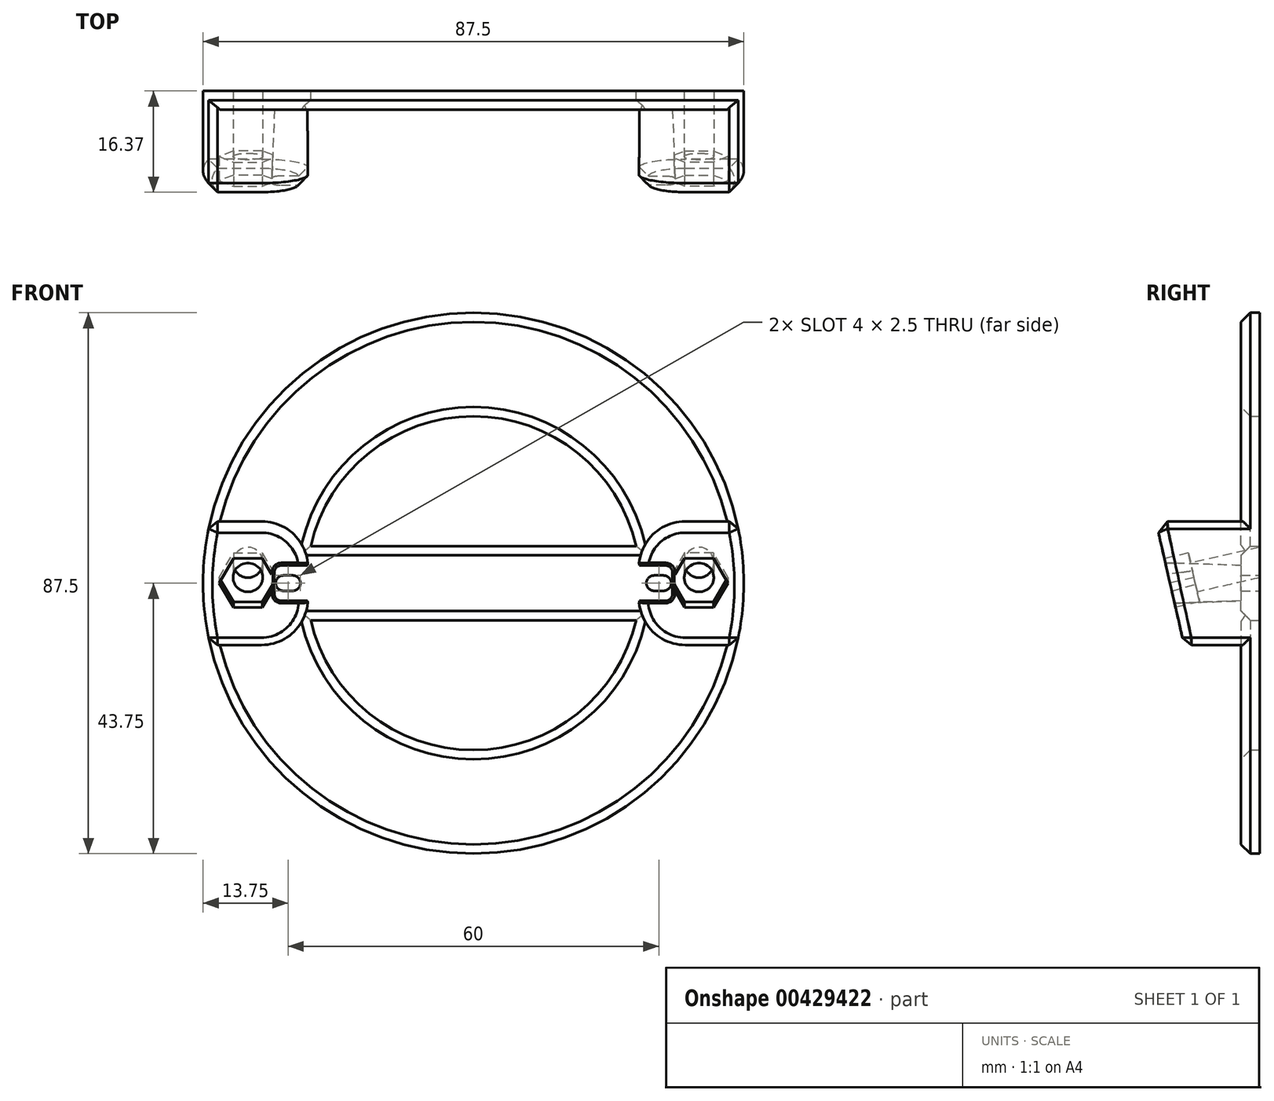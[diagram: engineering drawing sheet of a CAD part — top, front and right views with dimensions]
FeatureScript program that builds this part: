
annotation { "Feature Type Name" : "Feature", "Feature Type Description" : "" }
export const myFeature = defineFeature(function(context is Context, id is Id, definition is map)
    precondition{}
    {
        {
            var Q0;
            Q0=qCreatedBy(makeId("Front.planeOp"),FACE);
            var sketch = newSketch(context, id + "F0", { "sketchPlane" : qUnion([Q0])});
            skCircle(sketch, "E0", {"center": v(0, 0) * mm, "radius": 43.75 * mm});
            skCircle(sketch, "E1", {"center": v(0, 0) * mm, "radius": 24 * mm});
            skSolve(sketch);
        }
        {
            var Q0;
            Q0=makeQuery(id+"F0.imprint","IMPRINT",FACE,{"disambiguationData":[TD([[makeQuery(id+"F0.imprint","IMPRINT",EDGE,{"derivedFrom":sQuery(id+"F0.wireOp",EDGE,"E0")}),1.0]])]});
            extrude(context, id + "F1", {"entities" : qUnion([Q0]), "depth" : 30 * mm});
        }
        {
            var Q0;
            Q0=qCreatedBy(makeId("Right.planeOp"),FACE);
            var sketch = newSketch(context, id + "F2", { "sketchPlane" : qUnion([Q0])});
            skLineSegment(sketch, "E2", {"start": v(0, 43.75) * mm, "end": v(-24.5, 43.75) * mm});
            skLineSegment(sketch, "E3", {"start": v(-24.5, 43.75) * mm, "end": v(-4.5, -43.75) * mm});
            skLineSegment(sketch, "E4", {"start": v(-4.5, -43.75) * mm, "end": v(0, -43.75) * mm});
            skLineSegment(sketch, "E5", {"start": v(0, -43.75) * mm, "end": v(0, 43.75) * mm});
            skSolve(sketch);
        }
        {
            var Q0;
            Q0 = qSketchRegion(id + "F2", true);
            extrude(context, id + "F3", {"entities" : qUnion([Q0]), "endBound" : BoundingType.SYMMETRIC, "depth" : 90 * mm});
        }
        {
            var Q0;
            Q0=makeQuery(id+"F3.opExtrude","SWEPT_BODY",BODY,{"disambiguationData":[OSD([sQuery(id+"F2.wireOp",EDGE,"E2"),sQuery(id+"F2.wireOp",EDGE,"E3"),sQuery(id+"F2.wireOp",EDGE,"E4"),sQuery(id+"F2.wireOp",EDGE,"E5")])]});
            var Q1;
            Q1=makeQuery(id+"F1.opExtrude","SWEPT_BODY",BODY,{"disambiguationData":[OSD([sQuery(id+"F0.wireOp",EDGE,"E0"),sQuery(id+"F0.wireOp",EDGE,"E1")])]});
            booleanBodies(context, id + "F4", {"operationType" : BooleanOperationType.INTERSECTION, "tools" : qUnion([Q0, Q1])});
        }
        {
            var Q0;
            Q0=qCreatedBy(makeId("Front.planeOp"),FACE);
            var sketch = newSketch(context, id + "F5", { "sketchPlane" : qUnion([Q0])});
            skLineSegment(sketch, "E6.bottom", {"start": v(-50, 10) * mm, "end": v(50, 10) * mm});
            skLineSegment(sketch, "E6.top", {"start": v(-50, -10) * mm, "end": v(50, -10) * mm});
            skLineSegment(sketch, "E6.left", {"start": v(-50, 10) * mm, "end": v(-50, -10) * mm});
            skLineSegment(sketch, "E6.right", {"start": v(50, 10) * mm, "end": v(50, -10) * mm});
            skCircle(sketch, "E7", {"center": v(0, 0) * mm, "radius": 27 * mm});
            skSolve(sketch);
        }
        {
            var Q0;
            {var subQ0=sQuery(id+"F5.wireOp",EDGE,"E6.left");Q0=makeQuery(id+"F5.imprint","IMPRINT",FACE,{"disambiguationData":[TD([[makeQuery(id+"F5.imprint","IMPRINT",EDGE,{"derivedFrom":subQ0}),1.0]])]});}
            var Q1;
            {var subQ0=sQuery(id+"F5.wireOp",EDGE,"E6.right");Q1=makeQuery(id+"F5.imprint","IMPRINT",FACE,{"disambiguationData":[TD([[makeQuery(id+"F5.imprint","IMPRINT",EDGE,{"derivedFrom":subQ0}),-1.0]])]});}
            extrude(context, id + "F6", {"entities" : qUnion([Q0, Q1]), "depth" : 30 * mm});
        }
        {
            var Q0;
            Q0=makeQuery(id+"F6.opExtrude","SWEPT_BODY",BODY,{"disambiguationData":[OSD([sQuery(id+"F5.wireOp",EDGE,"E6.bottom"),sQuery(id+"F5.wireOp",EDGE,"E6.top"),sQuery(id+"F5.wireOp",EDGE,"E6.left"),sQuery(id+"F5.wireOp",EDGE,"E7")])]});
            var Q1;
            Q1=makeQuery(id+"F4.opBoolean","INTERSECT",BODY,{"derivedFrom":[makeQuery(id+"F1.opExtrude","SWEPT_BODY",BODY,{"disambiguationData":[OSD([sQuery(id+"F0.wireOp",EDGE,"E0"),sQuery(id+"F0.wireOp",EDGE,"E1")])]}),makeQuery(id+"F3.opExtrude","SWEPT_BODY",BODY,{"disambiguationData":[OSD([sQuery(id+"F2.wireOp",EDGE,"E2"),sQuery(id+"F2.wireOp",EDGE,"E3"),sQuery(id+"F2.wireOp",EDGE,"E4"),sQuery(id+"F2.wireOp",EDGE,"E5")])]})]});
            booleanBodies(context, id + "F7", {"operationType" : BooleanOperationType.INTERSECTION, "tools" : qUnion([Q0, Q1]), "keepTools" : true});
        }
        {
            var Q0;
            Q0=makeQuery(id+"F4.opBoolean","INTERSECT",BODY,{"derivedFrom":[makeQuery(id+"F1.opExtrude","SWEPT_BODY",BODY,{"disambiguationData":[OSD([sQuery(id+"F0.wireOp",EDGE,"E0"),sQuery(id+"F0.wireOp",EDGE,"E1")])]}),makeQuery(id+"F3.opExtrude","SWEPT_BODY",BODY,{"disambiguationData":[OSD([sQuery(id+"F2.wireOp",EDGE,"E2"),sQuery(id+"F2.wireOp",EDGE,"E3"),sQuery(id+"F2.wireOp",EDGE,"E4"),sQuery(id+"F2.wireOp",EDGE,"E5")])]})]});
            var Q1;
            Q1=makeQuery(id+"F6.opExtrude","SWEPT_BODY",BODY,{"disambiguationData":[OSD([sQuery(id+"F5.wireOp",EDGE,"E6.bottom"),sQuery(id+"F5.wireOp",EDGE,"E6.top"),sQuery(id+"F5.wireOp",EDGE,"E6.right"),sQuery(id+"F5.wireOp",EDGE,"E7")])]});
            booleanBodies(context, id + "F8", {"operationType" : BooleanOperationType.INTERSECTION, "tools" : qUnion([Q0, Q1])});
        }
        {
            var Q0;
            Q0=qCreatedBy(makeId("Front.planeOp"),FACE);
            var sketch = newSketch(context, id + "F9", { "sketchPlane" : qUnion([Q0])});
            skCircle(sketch, "E8", {"center": v(0, 0) * mm, "radius": 43.75 * mm});
            skCircle(sketch, "E9", {"center": v(0, 0) * mm, "radius": 27 * mm});
            skLineSegment(sketch, "E10.bottom", {"start": v(-26.32, 6) * mm, "end": v(26.32, 6) * mm});
            skLineSegment(sketch, "E10.top", {"start": v(-26.32, -6) * mm, "end": v(26.32, -6) * mm});
            skPoint(sketch, "E11", {"position": v(-26.32, 6) * mm});
            skPoint(sketch, "E12", {"position": v(-26.32, -6) * mm});
            skPoint(sketch, "E13", {"position": v(26.32, 6) * mm});
            skPoint(sketch, "E14", {"position": v(26.32, -6) * mm});
            skSolve(sketch);
        }
        {
            var Q0;
            Q0=makeQuery(id+"F9.imprint","IMPRINT",FACE,{"disambiguationData":[TD([[makeQuery(id+"F9.imprint","IMPRINT",EDGE,{"derivedFrom":sQuery(id+"F9.wireOp",EDGE,"E8")}),1.0]])]});
            var Q1;
            {var subQ0=sQuery(id+"F9.wireOp",EDGE,"E10.bottom");Q1=makeQuery(id+"F9.imprint","IMPRINT",FACE,{"disambiguationData":[TD([[makeQuery(id+"F9.imprint","IMPRINT",EDGE,{"derivedFrom":subQ0}),-1.0]])]});}
            extrude(context, id + "F10", {"entities" : qUnion([Q0, Q1]), "depth" : 3 * mm});
        }
        {
            var Q0;
            Q0=qCreatedBy(makeId("Front.planeOp"),FACE);
            var sketch = newSketch(context, id + "F11", { "sketchPlane" : qUnion([Q0])});
            skLineSegment(sketch, "E15.bottom", {"start": v(-29.25, 1.25) * mm, "end": v(-30.75, 1.25) * mm});
            skLineSegment(sketch, "E15.top", {"start": v(-29.25, -1.25) * mm, "end": v(-30.75, -1.25) * mm});
            skLineSegment(sketch, "E15.left", {"start": v(-28, 0) * mm, "end": v(-28, 0) * mm});
            skLineSegment(sketch, "E15.right", {"start": v(-32, 0) * mm, "end": v(-32, 0) * mm});
            skPoint(sketch, "E15.middle", {"position": v(-30, 0) * mm});
            skPoint(sketch, "E16.visualSharp", {"position": v(-28, 1.25) * mm});
            skArc(sketch, "E16.filletArc", {"start": v(-28, 0) * mm, "mid": v(-28.37, 0.88) * mm, "end": v(-29.25, 1.25) * mm});
            skPoint(sketch, "E17.visualSharp", {"position": v(-32, 1.25) * mm});
            skArc(sketch, "E17.filletArc", {"start": v(-30.75, 1.25) * mm, "mid": v(-31.63, 0.88) * mm, "end": v(-32, 0) * mm});
            skPoint(sketch, "E18.visualSharp", {"position": v(-32, -1.25) * mm});
            skArc(sketch, "E18.filletArc", {"start": v(-32, 0) * mm, "mid": v(-31.63, -0.88) * mm, "end": v(-30.75, -1.25) * mm});
            skPoint(sketch, "E19.visualSharp", {"position": v(-28, -1.25) * mm});
            skArc(sketch, "E19.filletArc", {"start": v(-29.25, -1.25) * mm, "mid": v(-28.37, -0.88) * mm, "end": v(-28, 0) * mm});
            skArc(sketch, "E20.MirrorCS", {"start": v(28, 0) * mm, "mid": v(28.37, 0.88) * mm, "end": v(29.25, 1.25) * mm});
            skArc(sketch, "E21.MirrorCS", {"start": v(29.25, -1.25) * mm, "mid": v(28.37, -0.88) * mm, "end": v(28, 0) * mm});
            skLineSegment(sketch, "E22.MirrorCS", {"start": v(29.25, -1.25) * mm, "end": v(30.75, -1.25) * mm});
            skLineSegment(sketch, "E23.MirrorCS", {"start": v(29.25, 1.25) * mm, "end": v(30.75, 1.25) * mm});
            skPoint(sketch, "E24.MirrorP", {"position": v(32, 1.25) * mm});
            skArc(sketch, "E25.MirrorCS", {"start": v(30.75, 1.25) * mm, "mid": v(31.63, 0.88) * mm, "end": v(32, 0) * mm});
            skArc(sketch, "E26.MirrorCS", {"start": v(32, 0) * mm, "mid": v(31.63, -0.88) * mm, "end": v(30.75, -1.25) * mm});
            skPoint(sketch, "E27.MirrorP", {"position": v(32, -1.25) * mm});
            skPoint(sketch, "E28.MirrorP", {"position": v(28, -1.25) * mm});
            skPoint(sketch, "E29.MirrorP", {"position": v(28, 1.25) * mm});
            skSolve(sketch);
        }
        {
            var Q0;
            Q0 = qSketchRegion(id + "F11", true);
            extrude(context, id + "F12", {"entities" : qUnion([Q0]), "depth" : 25 * mm});
        }
        {
            var Q0;
            Q0=makeQuery(id+"F6.opExtrude","SWEPT_BODY",BODY,{"disambiguationData":[OSD([sQuery(id+"F5.wireOp",EDGE,"E6.bottom"),sQuery(id+"F5.wireOp",EDGE,"E6.top"),sQuery(id+"F5.wireOp",EDGE,"E6.left"),sQuery(id+"F5.wireOp",EDGE,"E7")])]});
            deleteBodies(context, id + "F13", {"entities" : qUnion([Q0])});
        }
        {
            var Q0;
            Q0=qCreatedBy(makeId("Front.planeOp"),FACE);
            var sketch = newSketch(context, id + "F14", { "sketchPlane" : qUnion([Q0])});
            skLineSegment(sketch, "E30.bottom", {"start": v(-26.55, 2.75) * mm, "end": v(-31.11, 2.75) * mm});
            skLineSegment(sketch, "E30.top", {"start": v(-26.55, -2.75) * mm, "end": v(-31.11, -2.75) * mm});
            skLineSegment(sketch, "E30.left", {"start": v(-24.55, 0.75) * mm, "end": v(-24.55, -0.75) * mm});
            skLineSegment(sketch, "E30.right", {"start": v(-32.11, 1.75) * mm, "end": v(-32.11, -1.75) * mm});
            skPoint(sketch, "E30.middle", {"position": v(-28.33, 0) * mm});
            skPoint(sketch, "E31.visualSharp", {"position": v(-24.55, 2.75) * mm});
            skArc(sketch, "E31.filletArc", {"start": v(-24.55, 0.75) * mm, "mid": v(-25.13, 2.16) * mm, "end": v(-26.55, 2.75) * mm});
            skPoint(sketch, "E32.visualSharp", {"position": v(-24.55, -2.75) * mm});
            skArc(sketch, "E32.filletArc", {"start": v(-26.55, -2.75) * mm, "mid": v(-25.13, -2.16) * mm, "end": v(-24.55, -0.75) * mm});
            skPoint(sketch, "E33.visualSharp", {"position": v(-32.11, -2.75) * mm});
            skArc(sketch, "E33.filletArc", {"start": v(-32.11, -1.75) * mm, "mid": v(-31.82, -2.46) * mm, "end": v(-31.11, -2.75) * mm});
            skPoint(sketch, "E34.visualSharp", {"position": v(-32.11, 2.75) * mm});
            skArc(sketch, "E34.filletArc", {"start": v(-31.11, 2.75) * mm, "mid": v(-31.82, 2.46) * mm, "end": v(-32.11, 1.75) * mm});
            skArc(sketch, "E35.MirrorCS", {"start": v(31.11, 2.75) * mm, "mid": v(31.82, 2.46) * mm, "end": v(32.11, 1.75) * mm});
            skLineSegment(sketch, "E36.MirrorCS", {"start": v(32.11, 1.75) * mm, "end": v(32.11, -1.75) * mm});
            skArc(sketch, "E37.MirrorCS", {"start": v(32.11, -1.75) * mm, "mid": v(31.82, -2.46) * mm, "end": v(31.11, -2.75) * mm});
            skLineSegment(sketch, "E38.MirrorCS", {"start": v(26.55, 2.75) * mm, "end": v(31.11, 2.75) * mm});
            skLineSegment(sketch, "E39.MirrorCS", {"start": v(26.55, -2.75) * mm, "end": v(31.11, -2.75) * mm});
            skArc(sketch, "E40.MirrorCS", {"start": v(26.55, -2.75) * mm, "mid": v(25.13, -2.16) * mm, "end": v(24.55, -0.75) * mm});
            skArc(sketch, "E41.MirrorCS", {"start": v(24.55, 0.75) * mm, "mid": v(25.13, 2.16) * mm, "end": v(26.55, 2.75) * mm});
            skSolve(sketch);
        }
        {
            var Q0;
            Q0 = qSketchRegion(id + "F14", true);
            extrude(context, id + "F15", {"entities" : qUnion([Q0]), "depth" : 25 * mm, "hasDraft" : true, "draftAngle" : 2 * degree});
        }
        {
            var Q0;
            Q0=makeQuery(id+"F15.opExtrude","SWEPT_BODY",BODY,{"disambiguationData":[OSD([sQuery(id+"F14.wireOp",EDGE,"E30.bottom"),sQuery(id+"F14.wireOp",EDGE,"E30.top"),sQuery(id+"F14.wireOp",EDGE,"E30.left"),sQuery(id+"F14.wireOp",EDGE,"E30.right"),sQuery(id+"F14.wireOp",EDGE,"E31.filletArc"),sQuery(id+"F14.wireOp",EDGE,"E32.filletArc"),sQuery(id+"F14.wireOp",EDGE,"E33.filletArc"),sQuery(id+"F14.wireOp",EDGE,"E34.filletArc")])]});
            var Q1;
            Q1=qCreatedBy(makeId("Right.planeOp"),FACE);
            mirror(context, id + "F16", {"entities" : qUnion([Q0]), "mirrorPlane" : qUnion([Q1])});
        }
        {
            var Q0;
            Q0=makeQuery(id+"F15.opExtrude","SWEPT_BODY",BODY,{"disambiguationData":[OSD([sQuery(id+"F14.wireOp",EDGE,"E30.bottom"),sQuery(id+"F14.wireOp",EDGE,"E30.top"),sQuery(id+"F14.wireOp",EDGE,"E30.left"),sQuery(id+"F14.wireOp",EDGE,"E30.right"),sQuery(id+"F14.wireOp",EDGE,"E31.filletArc"),sQuery(id+"F14.wireOp",EDGE,"E32.filletArc"),sQuery(id+"F14.wireOp",EDGE,"E33.filletArc"),sQuery(id+"F14.wireOp",EDGE,"E34.filletArc")])]});
            var Q1;
            Q1=makeQuery(id+"F7.opBoolean","INTERSECT",BODY,{"derivedFrom":[makeQuery(id+"F4.opBoolean","INTERSECT",BODY,{"derivedFrom":[makeQuery(id+"F1.opExtrude","SWEPT_BODY",BODY,{"disambiguationData":[OSD([sQuery(id+"F0.wireOp",EDGE,"E0"),sQuery(id+"F0.wireOp",EDGE,"E1")])]}),makeQuery(id+"F3.opExtrude","SWEPT_BODY",BODY,{"disambiguationData":[OSD([sQuery(id+"F2.wireOp",EDGE,"E2"),sQuery(id+"F2.wireOp",EDGE,"E3"),sQuery(id+"F2.wireOp",EDGE,"E4"),sQuery(id+"F2.wireOp",EDGE,"E5")])]})]}),makeQuery(id+"F6.opExtrude","SWEPT_BODY",BODY,{"disambiguationData":[OSD([sQuery(id+"F5.wireOp",EDGE,"E6.bottom"),sQuery(id+"F5.wireOp",EDGE,"E6.top"),sQuery(id+"F5.wireOp",EDGE,"E6.left"),sQuery(id+"F5.wireOp",EDGE,"E7")])]})]});
            booleanBodies(context, id + "F17", {"operationType" : BooleanOperationType.SUBTRACTION, "tools" : qUnion([Q0]), "targets" : qUnion([Q1])});
        }
        {
            var Q0;
            Q0=makeQuery(id+"F16.opPattern","COPY",BODY,{"derivedFrom":makeQuery(id+"F15.opExtrude","SWEPT_BODY",BODY,{"disambiguationData":[OSD([sQuery(id+"F14.wireOp",EDGE,"E30.bottom"),sQuery(id+"F14.wireOp",EDGE,"E30.top"),sQuery(id+"F14.wireOp",EDGE,"E30.left"),sQuery(id+"F14.wireOp",EDGE,"E30.right"),sQuery(id+"F14.wireOp",EDGE,"E31.filletArc"),sQuery(id+"F14.wireOp",EDGE,"E32.filletArc"),sQuery(id+"F14.wireOp",EDGE,"E33.filletArc"),sQuery(id+"F14.wireOp",EDGE,"E34.filletArc")])]}),"instanceName":"1"});
            var Q1;
            Q1=makeQuery(id+"F8.opBoolean","INTERSECT",BODY,{"derivedFrom":[makeQuery(id+"F4.opBoolean","INTERSECT",BODY,{"derivedFrom":[makeQuery(id+"F1.opExtrude","SWEPT_BODY",BODY,{"disambiguationData":[OSD([sQuery(id+"F0.wireOp",EDGE,"E0"),sQuery(id+"F0.wireOp",EDGE,"E1")])]}),makeQuery(id+"F3.opExtrude","SWEPT_BODY",BODY,{"disambiguationData":[OSD([sQuery(id+"F2.wireOp",EDGE,"E2"),sQuery(id+"F2.wireOp",EDGE,"E3"),sQuery(id+"F2.wireOp",EDGE,"E4"),sQuery(id+"F2.wireOp",EDGE,"E5")])]})]}),makeQuery(id+"F6.opExtrude","SWEPT_BODY",BODY,{"disambiguationData":[OSD([sQuery(id+"F5.wireOp",EDGE,"E6.bottom"),sQuery(id+"F5.wireOp",EDGE,"E6.top"),sQuery(id+"F5.wireOp",EDGE,"E6.right"),sQuery(id+"F5.wireOp",EDGE,"E7")])]})]});
            booleanBodies(context, id + "F18", {"operationType" : BooleanOperationType.SUBTRACTION, "tools" : qUnion([Q0]), "targets" : qUnion([Q1])});
        }
        {
            var Q0;
            Q0=makeQuery(id+"F12.opExtrude","SWEPT_BODY",BODY,{"disambiguationData":[OSD([sQuery(id+"F11.wireOp",EDGE,"E15.bottom"),sQuery(id+"F11.wireOp",EDGE,"E15.top"),sQuery(id+"F11.wireOp",EDGE,"E16.filletArc"),sQuery(id+"F11.wireOp",EDGE,"E17.filletArc"),sQuery(id+"F11.wireOp",EDGE,"E18.filletArc"),sQuery(id+"F11.wireOp",EDGE,"E19.filletArc")])]});
            var Q1;
            Q1=makeQuery(id+"F12.opExtrude","SWEPT_BODY",BODY,{"disambiguationData":[OSD([sQuery(id+"F11.wireOp",EDGE,"E20.MirrorCS"),sQuery(id+"F11.wireOp",EDGE,"E21.MirrorCS"),sQuery(id+"F11.wireOp",EDGE,"E22.MirrorCS"),sQuery(id+"F11.wireOp",EDGE,"E23.MirrorCS"),sQuery(id+"F11.wireOp",EDGE,"E25.MirrorCS"),sQuery(id+"F11.wireOp",EDGE,"E26.MirrorCS")])]});
            var Q2;
            Q2=makeQuery(id+"F10.opExtrude","SWEPT_BODY",BODY,{"disambiguationData":[OSD([sQuery(id+"F9.wireOp",EDGE,"E8"),sQuery(id+"F9.wireOp",EDGE,"E9"),sQuery(id+"F9.wireOp",EDGE,"E10.bottom"),sQuery(id+"F9.wireOp",EDGE,"E10.top")])]});
            booleanBodies(context, id + "F19", {"operationType" : BooleanOperationType.SUBTRACTION, "tools" : qUnion([Q0, Q1]), "targets" : qUnion([Q2])});
        }
        {
            var Q0;
            Q0=makeQuery(id+"F7.opBoolean","COPY",FACE,{"derivedFrom":makeQuery(id+"F3.opExtrude","SWEPT_FACE",FACE,{"disambiguationData":[OSD([sQuery(id+"F2.wireOp",EDGE,"E3")])]})});
            var sketch = newSketch(context, id + "F20", { "sketchPlane" : qUnion([Q0])});
            skCircle(sketch, "E42.cCircle", {"center": v(-36.5, 3.27) * mm, "radius": 4.05 * mm, "construction": true});
            skLineSegment(sketch, "E42.0", {"start": v(-38.84, 7.32) * mm, "end": v(-34.16, 7.32) * mm});
            skLineSegment(sketch, "E42.1", {"start": v(-34.16, 7.32) * mm, "end": v(-31.82, 3.27) * mm});
            skLineSegment(sketch, "E42.2", {"start": v(-31.82, 3.27) * mm, "end": v(-34.16, -0.78) * mm});
            skLineSegment(sketch, "E42.3", {"start": v(-34.16, -0.78) * mm, "end": v(-38.84, -0.78) * mm});
            skLineSegment(sketch, "E42.4", {"start": v(-38.84, -0.78) * mm, "end": v(-41.18, 3.27) * mm});
            skLineSegment(sketch, "E42.5", {"start": v(-41.18, 3.27) * mm, "end": v(-38.84, 7.32) * mm});
            skPoint(sketch, "E42.0.midPoint", {"position": v(-36.5, 7.32) * mm});
            skSolve(sketch);
        }
        {
            var Q0;
            Q0 = qSketchRegion(id + "F20", true);
            extrude(context, id + "F21", {"entities" : qUnion([Q0]), "operationType" : NewBodyOperationType.REMOVE, "oppositeDirection" : true, "depth" : 4 * mm});
        }
        {
            var Q0;
            Q0=makeQuery(id+"F7.opBoolean","INTERSECT",BODY,{"derivedFrom":[makeQuery(id+"F4.opBoolean","INTERSECT",BODY,{"derivedFrom":[makeQuery(id+"F1.opExtrude","SWEPT_BODY",BODY,{"disambiguationData":[OSD([sQuery(id+"F0.wireOp",EDGE,"E0"),sQuery(id+"F0.wireOp",EDGE,"E1")])]}),makeQuery(id+"F3.opExtrude","SWEPT_BODY",BODY,{"disambiguationData":[OSD([sQuery(id+"F2.wireOp",EDGE,"E2"),sQuery(id+"F2.wireOp",EDGE,"E3"),sQuery(id+"F2.wireOp",EDGE,"E4"),sQuery(id+"F2.wireOp",EDGE,"E5")])]})]}),makeQuery(id+"F6.opExtrude","SWEPT_BODY",BODY,{"disambiguationData":[OSD([sQuery(id+"F5.wireOp",EDGE,"E6.bottom"),sQuery(id+"F5.wireOp",EDGE,"E6.top"),sQuery(id+"F5.wireOp",EDGE,"E6.left"),sQuery(id+"F5.wireOp",EDGE,"E7")])]})]});
            var Q1;
            Q1=qCreatedBy(makeId("Right.planeOp"),FACE);
            mirror(context, id + "F22", {"entities" : qUnion([Q0]), "mirrorPlane" : qUnion([Q1])});
        }
        {
            var Q0;
            Q0=makeQuery(id+"F8.opBoolean","INTERSECT",BODY,{"derivedFrom":[makeQuery(id+"F4.opBoolean","INTERSECT",BODY,{"derivedFrom":[makeQuery(id+"F1.opExtrude","SWEPT_BODY",BODY,{"disambiguationData":[OSD([sQuery(id+"F0.wireOp",EDGE,"E0"),sQuery(id+"F0.wireOp",EDGE,"E1")])]}),makeQuery(id+"F3.opExtrude","SWEPT_BODY",BODY,{"disambiguationData":[OSD([sQuery(id+"F2.wireOp",EDGE,"E2"),sQuery(id+"F2.wireOp",EDGE,"E3"),sQuery(id+"F2.wireOp",EDGE,"E4"),sQuery(id+"F2.wireOp",EDGE,"E5")])]})]}),makeQuery(id+"F6.opExtrude","SWEPT_BODY",BODY,{"disambiguationData":[OSD([sQuery(id+"F5.wireOp",EDGE,"E6.bottom"),sQuery(id+"F5.wireOp",EDGE,"E6.top"),sQuery(id+"F5.wireOp",EDGE,"E6.right"),sQuery(id+"F5.wireOp",EDGE,"E7")])]})]});
            deleteBodies(context, id + "F23", {"entities" : qUnion([Q0])});
        }
        {
            var Q0;
            Q0=makeQuery(id+"F7.opBoolean","COPY",FACE,{"derivedFrom":makeQuery(id+"F3.opExtrude","SWEPT_FACE",FACE,{"disambiguationData":[OSD([sQuery(id+"F2.wireOp",EDGE,"E3")])]})});
            var sketch = newSketch(context, id + "F24", { "sketchPlane" : qUnion([Q0])});
            skCircle(sketch, "E43", {"center": v(-36.5, 3.27) * mm, "radius": 2.4 * mm});
            skCircle(sketch, "E44.MirrorC", {"center": v(36.5, 3.27) * mm, "radius": 2.4 * mm});
            skSolve(sketch);
        }
        {
            var Q0;
            Q0 = qSketchRegion(id + "F24", true);
            extrude(context, id + "F25", {"entities" : qUnion([Q0]), "oppositeDirection" : true, "depth" : 17 * mm});
        }
        {
            var Q0;
            {var subQ0=sQuery(id+"F5.wireOp",EDGE,"E7");var subQ1=sQuery(id+"F5.wireOp",EDGE,"E6.bottom");Q0=makeQuery(id+"F22.opPattern","COPY",EDGE,{"derivedFrom":makeQuery(id+"F7.opBoolean","COPY",EDGE,{"derivedFrom":makeQuery(id+"F6.opExtrude","SWEPT_EDGE",EDGE,{"disambiguationData":[OSD([subQ1,subQ0]),TDD([makeQuery(id+"F5.imprint","INTERSECT",VERTEX,{"disambiguationData":[OD(0.0)],"derivedFrom":[subQ1,subQ0]})])]})}),"instanceName":"1"});}
            var Q1;
            {var subQ0=sQuery(id+"F5.wireOp",EDGE,"E7");var subQ1=sQuery(id+"F5.wireOp",EDGE,"E6.top");Q1=makeQuery(id+"F22.opPattern","COPY",EDGE,{"derivedFrom":makeQuery(id+"F7.opBoolean","COPY",EDGE,{"derivedFrom":makeQuery(id+"F6.opExtrude","SWEPT_EDGE",EDGE,{"disambiguationData":[OSD([subQ1,subQ0]),TDD([makeQuery(id+"F5.imprint","INTERSECT",VERTEX,{"disambiguationData":[OD(0.0)],"derivedFrom":[subQ1,subQ0]})])]})}),"instanceName":"1"});}
            var Q2;
            {var subQ0=sQuery(id+"F5.wireOp",EDGE,"E7");var subQ1=sQuery(id+"F5.wireOp",EDGE,"E6.bottom");Q2=makeQuery(id+"F7.opBoolean","COPY",EDGE,{"derivedFrom":makeQuery(id+"F6.opExtrude","SWEPT_EDGE",EDGE,{"disambiguationData":[OSD([subQ1,subQ0]),TDD([makeQuery(id+"F5.imprint","INTERSECT",VERTEX,{"disambiguationData":[OD(0.0)],"derivedFrom":[subQ1,subQ0]})])]})});}
            var Q3;
            {var subQ0=sQuery(id+"F5.wireOp",EDGE,"E7");var subQ1=sQuery(id+"F5.wireOp",EDGE,"E6.top");Q3=makeQuery(id+"F7.opBoolean","COPY",EDGE,{"derivedFrom":makeQuery(id+"F6.opExtrude","SWEPT_EDGE",EDGE,{"disambiguationData":[OSD([subQ1,subQ0]),TDD([makeQuery(id+"F5.imprint","INTERSECT",VERTEX,{"disambiguationData":[OD(0.0)],"derivedFrom":[subQ1,subQ0]})])]})});}
            fillet(context, id + "F26", {"entities" : qUnion([Q0, Q1, Q2, Q3]), "radius" : 7.5 * mm, "tangentPropagation" : true, "allowEdgeOverflow" : false});
        }
        {
            var Q0;
            Q0=makeQuery(id+"F10.opExtrude","SWEPT_BODY",BODY,{"disambiguationData":[OSD([sQuery(id+"F9.wireOp",EDGE,"E8"),sQuery(id+"F9.wireOp",EDGE,"E9"),sQuery(id+"F9.wireOp",EDGE,"E10.bottom"),sQuery(id+"F9.wireOp",EDGE,"E10.top")])]});
            var Q1;
            Q1=makeQuery(id+"F7.opBoolean","INTERSECT",BODY,{"derivedFrom":[makeQuery(id+"F4.opBoolean","INTERSECT",BODY,{"derivedFrom":[makeQuery(id+"F1.opExtrude","SWEPT_BODY",BODY,{"disambiguationData":[OSD([sQuery(id+"F0.wireOp",EDGE,"E0"),sQuery(id+"F0.wireOp",EDGE,"E1")])]}),makeQuery(id+"F3.opExtrude","SWEPT_BODY",BODY,{"disambiguationData":[OSD([sQuery(id+"F2.wireOp",EDGE,"E2"),sQuery(id+"F2.wireOp",EDGE,"E3"),sQuery(id+"F2.wireOp",EDGE,"E4"),sQuery(id+"F2.wireOp",EDGE,"E5")])]})]}),makeQuery(id+"F6.opExtrude","SWEPT_BODY",BODY,{"disambiguationData":[OSD([sQuery(id+"F5.wireOp",EDGE,"E6.bottom"),sQuery(id+"F5.wireOp",EDGE,"E6.top"),sQuery(id+"F5.wireOp",EDGE,"E6.left"),sQuery(id+"F5.wireOp",EDGE,"E7")])]})]});
            var Q2;
            Q2=makeQuery(id+"F22.opPattern","COPY",BODY,{"derivedFrom":makeQuery(id+"F7.opBoolean","INTERSECT",BODY,{"derivedFrom":[makeQuery(id+"F4.opBoolean","INTERSECT",BODY,{"derivedFrom":[makeQuery(id+"F1.opExtrude","SWEPT_BODY",BODY,{"disambiguationData":[OSD([sQuery(id+"F0.wireOp",EDGE,"E0"),sQuery(id+"F0.wireOp",EDGE,"E1")])]}),makeQuery(id+"F3.opExtrude","SWEPT_BODY",BODY,{"disambiguationData":[OSD([sQuery(id+"F2.wireOp",EDGE,"E2"),sQuery(id+"F2.wireOp",EDGE,"E3"),sQuery(id+"F2.wireOp",EDGE,"E4"),sQuery(id+"F2.wireOp",EDGE,"E5")])]})]}),makeQuery(id+"F6.opExtrude","SWEPT_BODY",BODY,{"disambiguationData":[OSD([sQuery(id+"F5.wireOp",EDGE,"E6.bottom"),sQuery(id+"F5.wireOp",EDGE,"E6.top"),sQuery(id+"F5.wireOp",EDGE,"E6.left"),sQuery(id+"F5.wireOp",EDGE,"E7")])]})]}),"instanceName":"1"});
            booleanBodies(context, id + "F27", {"operationType" : BooleanOperationType.UNION, "tools" : qUnion([Q0, Q1, Q2])});
        }
        {
            var Q0;
            Q0=makeQuery(id+"F25.opExtrude","SWEPT_BODY",BODY,{"disambiguationData":[OSD([sQuery(id+"F24.wireOp",EDGE,"E43")])]});
            var Q1;
            Q1=makeQuery(id+"F25.opExtrude","SWEPT_BODY",BODY,{"disambiguationData":[OSD([sQuery(id+"F24.wireOp",EDGE,"E44.MirrorC")])]});
            var Q2;
            Q2=makeQuery(id+"F10.opExtrude","SWEPT_BODY",BODY,{"disambiguationData":[OSD([sQuery(id+"F9.wireOp",EDGE,"E8"),sQuery(id+"F9.wireOp",EDGE,"E9"),sQuery(id+"F9.wireOp",EDGE,"E10.bottom"),sQuery(id+"F9.wireOp",EDGE,"E10.top")])]});
            booleanBodies(context, id + "F28", {"operationType" : BooleanOperationType.SUBTRACTION, "tools" : qUnion([Q0, Q1]), "targets" : qUnion([Q2])});
        }
        {
            var Q0;
            {var subQ0=sQuery(id+"F9.wireOp",EDGE,"E8");var subQ1=sQuery(id+"F5.wireOp",EDGE,"E6.bottom");var subQ2=makeQuery(id+"F7.opBoolean","COPY",FACE,{"derivedFrom":makeQuery(id+"F6.opExtrude","SWEPT_FACE",FACE,{"disambiguationData":[OSD([subQ1]),TDD([makeQuery(id+"F5.imprint","IMPRINT",EDGE,{"disambiguationData":[TD([[makeQuery(id+"F5.imprint","INTERSECT",VERTEX,{"derivedFrom":[subQ1,sQuery(id+"F5.wireOp",EDGE,"E6.left")]}),-1.0]])],"derivedFrom":subQ1})])]})});Q0=makeQuery(id+"F27.opBoolean","SPLIT",EDGE,{"disambiguationData":[TD([subQ2])],"derivedFrom":makeQuery(id+"F10.opExtrude","CAP_EDGE",EDGE,{"disambiguationData":[OSD([subQ0])],"isStart":false})});}
            var Q1;
            {var subQ0=sQuery(id+"F9.wireOp",EDGE,"E8");var subQ1=sQuery(id+"F5.wireOp",EDGE,"E6.top");var subQ2=makeQuery(id+"F7.opBoolean","COPY",FACE,{"derivedFrom":makeQuery(id+"F6.opExtrude","SWEPT_FACE",FACE,{"disambiguationData":[OSD([subQ1]),TDD([makeQuery(id+"F5.imprint","IMPRINT",EDGE,{"disambiguationData":[TD([[makeQuery(id+"F5.imprint","INTERSECT",VERTEX,{"derivedFrom":[subQ1,sQuery(id+"F5.wireOp",EDGE,"E6.left")]}),-1.0]])],"derivedFrom":subQ1})])]})});Q1=makeQuery(id+"F27.opBoolean","SPLIT",EDGE,{"disambiguationData":[TD([subQ2])],"derivedFrom":makeQuery(id+"F10.opExtrude","CAP_EDGE",EDGE,{"disambiguationData":[OSD([subQ0])],"isStart":false})});}
            var Q2;
            {var subQ0=sQuery(id+"F9.wireOp",EDGE,"E10.bottom");var subQ1=sQuery(id+"F9.wireOp",EDGE,"E9");Q2=makeQuery(id+"F10.opExtrude","CAP_EDGE",EDGE,{"disambiguationData":[OSD([subQ1]),TDD([makeQuery(id+"F9.imprint","IMPRINT",EDGE,{"disambiguationData":[TD([[makeQuery(id+"F9.imprint","INTERSECT",VERTEX,{"disambiguationData":[OD(0.0)],"derivedFrom":[subQ1,subQ0]}),1.0]])],"derivedFrom":subQ1})])],"isStart":false});}
            var Q3;
            Q3=makeQuery(id+"F10.opExtrude","CAP_EDGE",EDGE,{"disambiguationData":[OSD([sQuery(id+"F9.wireOp",EDGE,"E10.bottom")])],"isStart":false});
            var Q4;
            Q4=makeQuery(id+"F10.opExtrude","CAP_EDGE",EDGE,{"disambiguationData":[OSD([sQuery(id+"F9.wireOp",EDGE,"E10.top")])],"isStart":false});
            var Q5;
            {var subQ0=sQuery(id+"F9.wireOp",EDGE,"E10.top");var subQ1=sQuery(id+"F9.wireOp",EDGE,"E9");Q5=makeQuery(id+"F10.opExtrude","CAP_EDGE",EDGE,{"disambiguationData":[OSD([subQ1]),TDD([makeQuery(id+"F9.imprint","IMPRINT",EDGE,{"disambiguationData":[TD([[makeQuery(id+"F9.imprint","INTERSECT",VERTEX,{"disambiguationData":[OD(0.0)],"derivedFrom":[subQ1,subQ0]}),-1.0]])],"derivedFrom":subQ1})])],"isStart":false});}
            var Q6;
            {var subQ0=sQuery(id+"F5.wireOp",EDGE,"E6.bottom");Q6=makeQuery(id+"F22.opPattern","COPY",EDGE,{"derivedFrom":makeQuery(id+"F7.opBoolean","INTERSECT",EDGE,{"derivedFrom":[makeQuery(id+"F1.opExtrude","SWEPT_FACE",FACE,{"disambiguationData":[OSD([sQuery(id+"F0.wireOp",EDGE,"E0")])]}),makeQuery(id+"F6.opExtrude","SWEPT_FACE",FACE,{"disambiguationData":[OSD([subQ0]),TDD([makeQuery(id+"F5.imprint","IMPRINT",EDGE,{"disambiguationData":[TD([[makeQuery(id+"F5.imprint","INTERSECT",VERTEX,{"derivedFrom":[subQ0,sQuery(id+"F5.wireOp",EDGE,"E6.left")]}),-1.0]])],"derivedFrom":subQ0})])]})]}),"instanceName":"1"});}
            var Q7;
            Q7=makeQuery(id+"F22.opPattern","COPY",EDGE,{"derivedFrom":makeQuery(id+"F7.opBoolean","COPY",EDGE,{"derivedFrom":makeQuery(id+"F4.opBoolean","INTERSECT",EDGE,{"derivedFrom":[makeQuery(id+"F1.opExtrude","SWEPT_FACE",FACE,{"disambiguationData":[OSD([sQuery(id+"F0.wireOp",EDGE,"E0")])]}),makeQuery(id+"F3.opExtrude","SWEPT_FACE",FACE,{"disambiguationData":[OSD([sQuery(id+"F2.wireOp",EDGE,"E3")])]})]})}),"instanceName":"1"});
            var Q8;
            {var subQ0=sQuery(id+"F5.wireOp",EDGE,"E6.top");Q8=makeQuery(id+"F22.opPattern","COPY",EDGE,{"derivedFrom":makeQuery(id+"F7.opBoolean","INTERSECT",EDGE,{"derivedFrom":[makeQuery(id+"F1.opExtrude","SWEPT_FACE",FACE,{"disambiguationData":[OSD([sQuery(id+"F0.wireOp",EDGE,"E0")])]}),makeQuery(id+"F6.opExtrude","SWEPT_FACE",FACE,{"disambiguationData":[OSD([subQ0]),TDD([makeQuery(id+"F5.imprint","IMPRINT",EDGE,{"disambiguationData":[TD([[makeQuery(id+"F5.imprint","INTERSECT",VERTEX,{"derivedFrom":[subQ0,sQuery(id+"F5.wireOp",EDGE,"E6.left")]}),-1.0]])],"derivedFrom":subQ0})])]})]}),"instanceName":"1"});}
            var Q9;
            {var subQ0=sQuery(id+"F5.wireOp",EDGE,"E6.bottom");Q9=makeQuery(id+"F22.opPattern","COPY",EDGE,{"derivedFrom":makeQuery(id+"F7.opBoolean","INTERSECT",EDGE,{"derivedFrom":[makeQuery(id+"F3.opExtrude","SWEPT_FACE",FACE,{"disambiguationData":[OSD([sQuery(id+"F2.wireOp",EDGE,"E3")])]}),makeQuery(id+"F6.opExtrude","SWEPT_FACE",FACE,{"disambiguationData":[OSD([subQ0]),TDD([makeQuery(id+"F5.imprint","IMPRINT",EDGE,{"disambiguationData":[TD([[makeQuery(id+"F5.imprint","INTERSECT",VERTEX,{"derivedFrom":[subQ0,sQuery(id+"F5.wireOp",EDGE,"E6.left")]}),-1.0]])],"derivedFrom":subQ0})])]})]}),"instanceName":"1"});}
            var Q10;
            {var subQ0=sQuery(id+"F5.wireOp",EDGE,"E7");var subQ1=sQuery(id+"F5.wireOp",EDGE,"E6.bottom");Q10=makeQuery(id+"F26.opFillet","BLEND_EDGE",EDGE,{"blendedFrom":[makeQuery(id+"F22.opPattern","COPY",EDGE,{"derivedFrom":makeQuery(id+"F7.opBoolean","COPY",EDGE,{"derivedFrom":makeQuery(id+"F6.opExtrude","SWEPT_EDGE",EDGE,{"disambiguationData":[OSD([subQ1,subQ0]),TDD([makeQuery(id+"F5.imprint","INTERSECT",VERTEX,{"disambiguationData":[OD(0.0)],"derivedFrom":[subQ1,subQ0]})])]})}),"instanceName":"1"}),makeQuery(id+"F22.opPattern","COPY",FACE,{"derivedFrom":makeQuery(id+"F7.opBoolean","COPY",FACE,{"derivedFrom":makeQuery(id+"F3.opExtrude","SWEPT_FACE",FACE,{"disambiguationData":[OSD([sQuery(id+"F2.wireOp",EDGE,"E3")])]})}),"instanceName":"1"})],"blendedInto":[makeQuery(id+"F22.opPattern","COPY",FACE,{"derivedFrom":makeQuery(id+"F7.opBoolean","COPY",FACE,{"derivedFrom":makeQuery(id+"F3.opExtrude","SWEPT_FACE",FACE,{"disambiguationData":[OSD([sQuery(id+"F2.wireOp",EDGE,"E3")])]})}),"instanceName":"1"})]});}
            var Q11;
            {var subQ0=sQuery(id+"F5.wireOp",EDGE,"E7");var subQ1=sQuery(id+"F5.wireOp",EDGE,"E6.top");Q11=makeQuery(id+"F26.opFillet","BLEND_EDGE",EDGE,{"blendedFrom":[makeQuery(id+"F22.opPattern","COPY",EDGE,{"derivedFrom":makeQuery(id+"F7.opBoolean","COPY",EDGE,{"derivedFrom":makeQuery(id+"F6.opExtrude","SWEPT_EDGE",EDGE,{"disambiguationData":[OSD([subQ1,subQ0]),TDD([makeQuery(id+"F5.imprint","INTERSECT",VERTEX,{"disambiguationData":[OD(0.0)],"derivedFrom":[subQ1,subQ0]})])]})}),"instanceName":"1"}),makeQuery(id+"F22.opPattern","COPY",FACE,{"derivedFrom":makeQuery(id+"F7.opBoolean","COPY",FACE,{"derivedFrom":makeQuery(id+"F3.opExtrude","SWEPT_FACE",FACE,{"disambiguationData":[OSD([sQuery(id+"F2.wireOp",EDGE,"E3")])]})}),"instanceName":"1"})],"blendedInto":[makeQuery(id+"F22.opPattern","COPY",FACE,{"derivedFrom":makeQuery(id+"F7.opBoolean","COPY",FACE,{"derivedFrom":makeQuery(id+"F3.opExtrude","SWEPT_FACE",FACE,{"disambiguationData":[OSD([sQuery(id+"F2.wireOp",EDGE,"E3")])]})}),"instanceName":"1"})]});}
            var Q12;
            {var subQ0=sQuery(id+"F5.wireOp",EDGE,"E6.top");Q12=makeQuery(id+"F22.opPattern","COPY",EDGE,{"derivedFrom":makeQuery(id+"F7.opBoolean","INTERSECT",EDGE,{"derivedFrom":[makeQuery(id+"F3.opExtrude","SWEPT_FACE",FACE,{"disambiguationData":[OSD([sQuery(id+"F2.wireOp",EDGE,"E3")])]}),makeQuery(id+"F6.opExtrude","SWEPT_FACE",FACE,{"disambiguationData":[OSD([subQ0]),TDD([makeQuery(id+"F5.imprint","IMPRINT",EDGE,{"disambiguationData":[TD([[makeQuery(id+"F5.imprint","INTERSECT",VERTEX,{"derivedFrom":[subQ0,sQuery(id+"F5.wireOp",EDGE,"E6.left")]}),-1.0]])],"derivedFrom":subQ0})])]})]}),"instanceName":"1"});}
            var Q13;
            {var subQ0=sQuery(id+"F5.wireOp",EDGE,"E6.bottom");Q13=makeQuery(id+"F7.opBoolean","INTERSECT",EDGE,{"derivedFrom":[makeQuery(id+"F1.opExtrude","SWEPT_FACE",FACE,{"disambiguationData":[OSD([sQuery(id+"F0.wireOp",EDGE,"E0")])]}),makeQuery(id+"F6.opExtrude","SWEPT_FACE",FACE,{"disambiguationData":[OSD([subQ0]),TDD([makeQuery(id+"F5.imprint","IMPRINT",EDGE,{"disambiguationData":[TD([[makeQuery(id+"F5.imprint","INTERSECT",VERTEX,{"derivedFrom":[subQ0,sQuery(id+"F5.wireOp",EDGE,"E6.left")]}),-1.0]])],"derivedFrom":subQ0})])]})]});}
            var Q14;
            {var subQ0=sQuery(id+"F5.wireOp",EDGE,"E6.bottom");Q14=makeQuery(id+"F7.opBoolean","INTERSECT",EDGE,{"derivedFrom":[makeQuery(id+"F3.opExtrude","SWEPT_FACE",FACE,{"disambiguationData":[OSD([sQuery(id+"F2.wireOp",EDGE,"E3")])]}),makeQuery(id+"F6.opExtrude","SWEPT_FACE",FACE,{"disambiguationData":[OSD([subQ0]),TDD([makeQuery(id+"F5.imprint","IMPRINT",EDGE,{"disambiguationData":[TD([[makeQuery(id+"F5.imprint","INTERSECT",VERTEX,{"derivedFrom":[subQ0,sQuery(id+"F5.wireOp",EDGE,"E6.left")]}),-1.0]])],"derivedFrom":subQ0})])]})]});}
            var Q15;
            {var subQ0=sQuery(id+"F5.wireOp",EDGE,"E7");var subQ1=sQuery(id+"F5.wireOp",EDGE,"E6.bottom");Q15=makeQuery(id+"F26.opFillet","BLEND_EDGE",EDGE,{"blendedFrom":[makeQuery(id+"F7.opBoolean","COPY",EDGE,{"derivedFrom":makeQuery(id+"F6.opExtrude","SWEPT_EDGE",EDGE,{"disambiguationData":[OSD([subQ1,subQ0]),TDD([makeQuery(id+"F5.imprint","INTERSECT",VERTEX,{"disambiguationData":[OD(0.0)],"derivedFrom":[subQ1,subQ0]})])]})}),makeQuery(id+"F7.opBoolean","COPY",FACE,{"derivedFrom":makeQuery(id+"F3.opExtrude","SWEPT_FACE",FACE,{"disambiguationData":[OSD([sQuery(id+"F2.wireOp",EDGE,"E3")])]})})],"blendedInto":[makeQuery(id+"F7.opBoolean","COPY",FACE,{"derivedFrom":makeQuery(id+"F3.opExtrude","SWEPT_FACE",FACE,{"disambiguationData":[OSD([sQuery(id+"F2.wireOp",EDGE,"E3")])]})})]});}
            var Q16;
            Q16=makeQuery(id+"F7.opBoolean","COPY",EDGE,{"derivedFrom":makeQuery(id+"F4.opBoolean","INTERSECT",EDGE,{"derivedFrom":[makeQuery(id+"F1.opExtrude","SWEPT_FACE",FACE,{"disambiguationData":[OSD([sQuery(id+"F0.wireOp",EDGE,"E0")])]}),makeQuery(id+"F3.opExtrude","SWEPT_FACE",FACE,{"disambiguationData":[OSD([sQuery(id+"F2.wireOp",EDGE,"E3")])]})]})});
            var Q17;
            {var subQ0=sQuery(id+"F5.wireOp",EDGE,"E6.top");Q17=makeQuery(id+"F7.opBoolean","INTERSECT",EDGE,{"derivedFrom":[makeQuery(id+"F3.opExtrude","SWEPT_FACE",FACE,{"disambiguationData":[OSD([sQuery(id+"F2.wireOp",EDGE,"E3")])]}),makeQuery(id+"F6.opExtrude","SWEPT_FACE",FACE,{"disambiguationData":[OSD([subQ0]),TDD([makeQuery(id+"F5.imprint","IMPRINT",EDGE,{"disambiguationData":[TD([[makeQuery(id+"F5.imprint","INTERSECT",VERTEX,{"derivedFrom":[subQ0,sQuery(id+"F5.wireOp",EDGE,"E6.left")]}),-1.0]])],"derivedFrom":subQ0})])]})]});}
            var Q18;
            {var subQ0=sQuery(id+"F5.wireOp",EDGE,"E7");var subQ1=sQuery(id+"F5.wireOp",EDGE,"E6.top");Q18=makeQuery(id+"F26.opFillet","BLEND_EDGE",EDGE,{"blendedFrom":[makeQuery(id+"F7.opBoolean","COPY",EDGE,{"derivedFrom":makeQuery(id+"F6.opExtrude","SWEPT_EDGE",EDGE,{"disambiguationData":[OSD([subQ1,subQ0]),TDD([makeQuery(id+"F5.imprint","INTERSECT",VERTEX,{"disambiguationData":[OD(0.0)],"derivedFrom":[subQ1,subQ0]})])]})}),makeQuery(id+"F7.opBoolean","COPY",FACE,{"derivedFrom":makeQuery(id+"F3.opExtrude","SWEPT_FACE",FACE,{"disambiguationData":[OSD([sQuery(id+"F2.wireOp",EDGE,"E3")])]})})],"blendedInto":[makeQuery(id+"F7.opBoolean","COPY",FACE,{"derivedFrom":makeQuery(id+"F3.opExtrude","SWEPT_FACE",FACE,{"disambiguationData":[OSD([sQuery(id+"F2.wireOp",EDGE,"E3")])]})})]});}
            var Q19;
            {var subQ0=sQuery(id+"F5.wireOp",EDGE,"E6.top");Q19=makeQuery(id+"F7.opBoolean","INTERSECT",EDGE,{"derivedFrom":[makeQuery(id+"F1.opExtrude","SWEPT_FACE",FACE,{"disambiguationData":[OSD([sQuery(id+"F0.wireOp",EDGE,"E0")])]}),makeQuery(id+"F6.opExtrude","SWEPT_FACE",FACE,{"disambiguationData":[OSD([subQ0]),TDD([makeQuery(id+"F5.imprint","IMPRINT",EDGE,{"disambiguationData":[TD([[makeQuery(id+"F5.imprint","INTERSECT",VERTEX,{"derivedFrom":[subQ0,sQuery(id+"F5.wireOp",EDGE,"E6.left")]}),-1.0]])],"derivedFrom":subQ0})])]})]});}
            chamfer(context, id + "F29", {"entities" : qUnion([Q0, Q1, Q2, Q3, Q4, Q5, Q6, Q7, Q8, Q9, Q10, Q11, Q12, Q13, Q14, Q15, Q16, Q17, Q18, Q19]), "width" : 1.5 * mm, "tangentPropagation" : true});
        }
    });
